# Revit family: BSM101
name_source: partatom
category: Modele ogólne
revit_build: Autodesk Revit 2015 (Build: 20140606_1530(x64)
units: mm (PartAtom-declared; Revit-internal decimal feet)

## types (4) — shared parameters
Autor = www.archispace.pl
Domyślna rzędna = 800 mm  [stored 2.62467 ft]
Grupa towarowa = PODAJNIKI PAPIERU TOALETOWEGO
Głębokość = 110 mm
Linia = MERIDA STELLA
Maksymalny wymiar roli = max. szer. 9 cm
Materiał obudowa = Merida_Stal_Matowa
Materiał obudowy = stal nierdzewna
Producent = MERIDA SP. Z O.O.
Rodzaj montażu = naścienny
Sposób podawania = z rolki
Szerokość = 325 mm  [stored 1.06627 ft]
Typ rolki = rolka Jumbo
URL = www.merida.com.pl
Wysokość = 285 mm  [stored 0.935039 ft]

## per-type parameters (varying)
| type | Kolor | Model | Opis | Strona produktu | Wielkość |
| BSM101 | matowa | Pojemnik na papier toaletowy MERIDA STELLA MAXI, matowy | BSM101 Pojemnik na papier toaletowy w roli. Maksymalna średnica roli 23 cm. Zamek bębenkowy zlicowany z powierzchnią. Łączenia boków spawane i szlifowane. Zawiasy ukryte. | www.sklep.merida.com.pl/produkt/5765/pojemnik-na-papier-toaletowy-merida-stella-maxi-stal-matowa | MIDI |
| BSP101 | polerowana | Pojemnik na papier toaletowy MERIDA STELLA MAXI, polerowany | BSP101 Pojemnik na papier toaletowy w roli. Maksymalna średnica roli 23 cm. Zamek bębenkowy zlicowany z powierzchnią. Łączenia boków spawane i szlifowane. Zawiasy ukryte. | www.sklep.merida.com.pl/produkt/2905/pojemnik-na-papier-toaletowy-merida-stella-maxi-stal-polerowana | MIDI |
| BSM202 | matowa | Pojemnik na papier toaletowy MERIDA STELLA DUO, matowy | BSM202 Pojemnik na papier toaletowy w roli. Maksymalna średnica roli 19 cm. Zamek bębenkowy zlicowany z powierzchnią. Łączenia boków spawane i szlifowane. Zawiasy ukryte. Dodatkowy  uchwyt na małą rolkę papieru (końcówkę rolki). | www.sklep.merida.com.pl/produkt/5735/pojemnik-na-papier-toaletowy-merida-stella-duo-z-uchwytem-na-resztke-rolki-papieru-stal-matowa | MINI |
| BSP202 | polerowana | Pojemnik na papier toaletowy MERIDA STELLA DUO, polerowany | BSP202 Pojemnik na papier toaletowy w roli. Maksymalna średnica roli 19 cm. Zamek bębenkowy zlicowany z powierzchnią. Łączenia boków spawane i szlifowane. Zawiasy ukryte. Dodatkowy  uchwyt na małą rolkę papieru (końcówkę rolki). | www.sklep.merida.com.pl/produkt/5832/pojemnik-na-papier-toaletowy-merida-stella-duo-z-uchwytem-na-resztke-rolki-stal-polerowana | MINI |

note: column(s) folded — value = type name in every type: Numer katalogowy

note: [stored X ft] marks values corroborated as IEEE doubles in the binary element streams (Revit-internal decimal feet)
